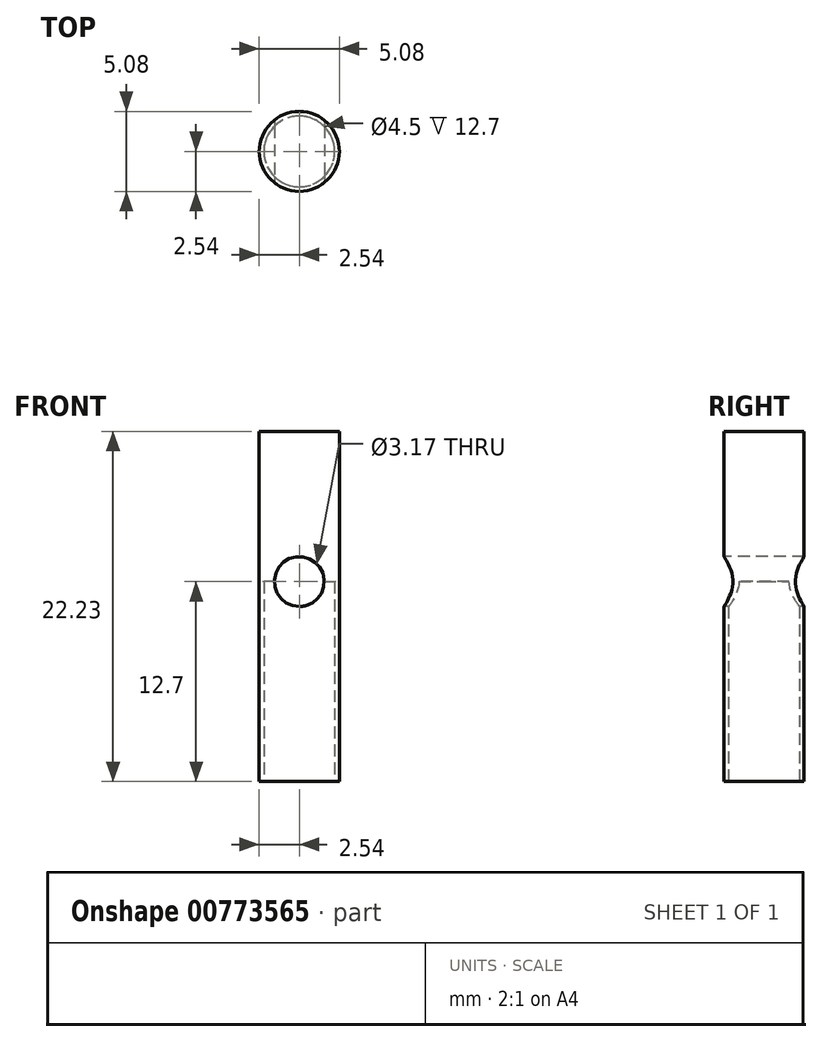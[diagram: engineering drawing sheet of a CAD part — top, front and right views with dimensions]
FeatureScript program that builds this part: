
annotation { "Feature Type Name" : "Feature", "Feature Type Description" : "" }
export const myFeature = defineFeature(function(context is Context, id is Id, definition is map)
    precondition{}
    {
        {
            var Q0;
            Q0=qCreatedBy(makeId("Top.planeOp"),FACE);
            var sketch = newSketch(context, id + "F0", { "sketchPlane" : qUnion([Q0])});
            skCircle(sketch, "E0", {"center": v(0, 0) * mm, "radius": 2.54 * mm});
            skPoint(sketch, "E1", {"position": v(0, 2.54) * mm});
            skPoint(sketch, "E2", {"position": v(0, -2.54) * mm});
            skPoint(sketch, "E3", {"position": v(-2.54, 0) * mm});
            skPoint(sketch, "E4", {"position": v(2.54, 0) * mm});
            skSolve(sketch);
        }
        {
            var Q0;
            Q0=makeQuery(id+"F0.imprint","IMPRINT",FACE,{"disambiguationData":[TD([[makeQuery(id+"F0.imprint","IMPRINT",EDGE,{"derivedFrom":sQuery(id+"F0.wireOp",EDGE,"E0")}),1.0]])]});
            extrude(context, id + "F1", {"entities" : qUnion([Q0]), "depth" : 22.22 * mm, "offsetDistance" : 25.4 * mm});
        }
        {
            var Q0;
            Q0=makeQuery(id+"F1.opExtrude","CAP_FACE",FACE,{"disambiguationData":[OSD([sQuery(id+"F0.wireOp",EDGE,"E0")])],"isStart":false});
            var sketch = newSketch(context, id + "F2", { "sketchPlane" : qUnion([Q0])});
            skPoint(sketch, "E5", {"position": v(0, -2.54) * mm});
            skPoint(sketch, "E6", {"position": v(0, 2.54) * mm});
            skPoint(sketch, "E7", {"position": v(-2.54, 0) * mm});
            skPoint(sketch, "E8", {"position": v(2.54, 0) * mm});
            skSolve(sketch);
        }
        {
            var Q0;
            Q0=sQuery(id+"F2.wireOp",VERTEX,"E5");
            var Q1;
            Q1=qCreatedBy(makeId("Front.planeOp"),FACE);
            cPlane(context, id + "F3", {"entities" : qUnion([Q0, Q1]), "cplaneType" : CPlaneType.PLANE_POINT, "offset" : 25.4 * mm, "width" : 152.4 * mm, "height" : 152.4 * mm});
        }
        {
            var Q0;
            Q0=qCreatedBy(id+"F3.planeOp",FACE);
            var sketch = newSketch(context, id + "F4", { "sketchPlane" : qUnion([Q0])});
            skCircle(sketch, "E9", {"center": v(0, 12.7) * mm, "radius": 1.59 * mm});
            skSolve(sketch);
        }
        {
            var Q0;
            Q0=sQuery(id+"F4.wireOp",VERTEX,"E9.center");
            var Q1;
            Q1=makeQuery(id+"F1.opExtrude","SWEPT_BODY",BODY,{"disambiguationData":[OSD([sQuery(id+"F0.wireOp",EDGE,"E0")])]});
            hole(context, id + "F5", {"style" : HoleStyle.SIMPLE, "endStyle" : HoleEndStyle.THROUGH, "holeDiameter" : 3.17 * mm, "majorDiameter" : 6.35 * mm, "tappedDepth" : 12.7 * mm, "tapClearance" : 3, "locations" : qUnion([Q0]), "scope" : qUnion([Q1])});
        }
        {
            var Q0;
            Q0=makeQuery(id+"F1.opExtrude","CAP_FACE",FACE,{"disambiguationData":[OSD([sQuery(id+"F0.wireOp",EDGE,"E0")])],"isStart":true});
            var sketch = newSketch(context, id + "F6", { "sketchPlane" : qUnion([Q0])});
            skCircle(sketch, "E10", {"center": v(0, 0) * mm, "radius": 2.25 * mm});
            skSolve(sketch);
        }
        {
            var Q0;
            Q0 = qSketchRegion(id + "F6", true);
            extrude(context, id + "F7", {"entities" : qUnion([Q0]), "operationType" : NewBodyOperationType.REMOVE, "oppositeDirection" : true, "depth" : 12.7 * mm, "offsetDistance" : 25.4 * mm});
        }
    });
